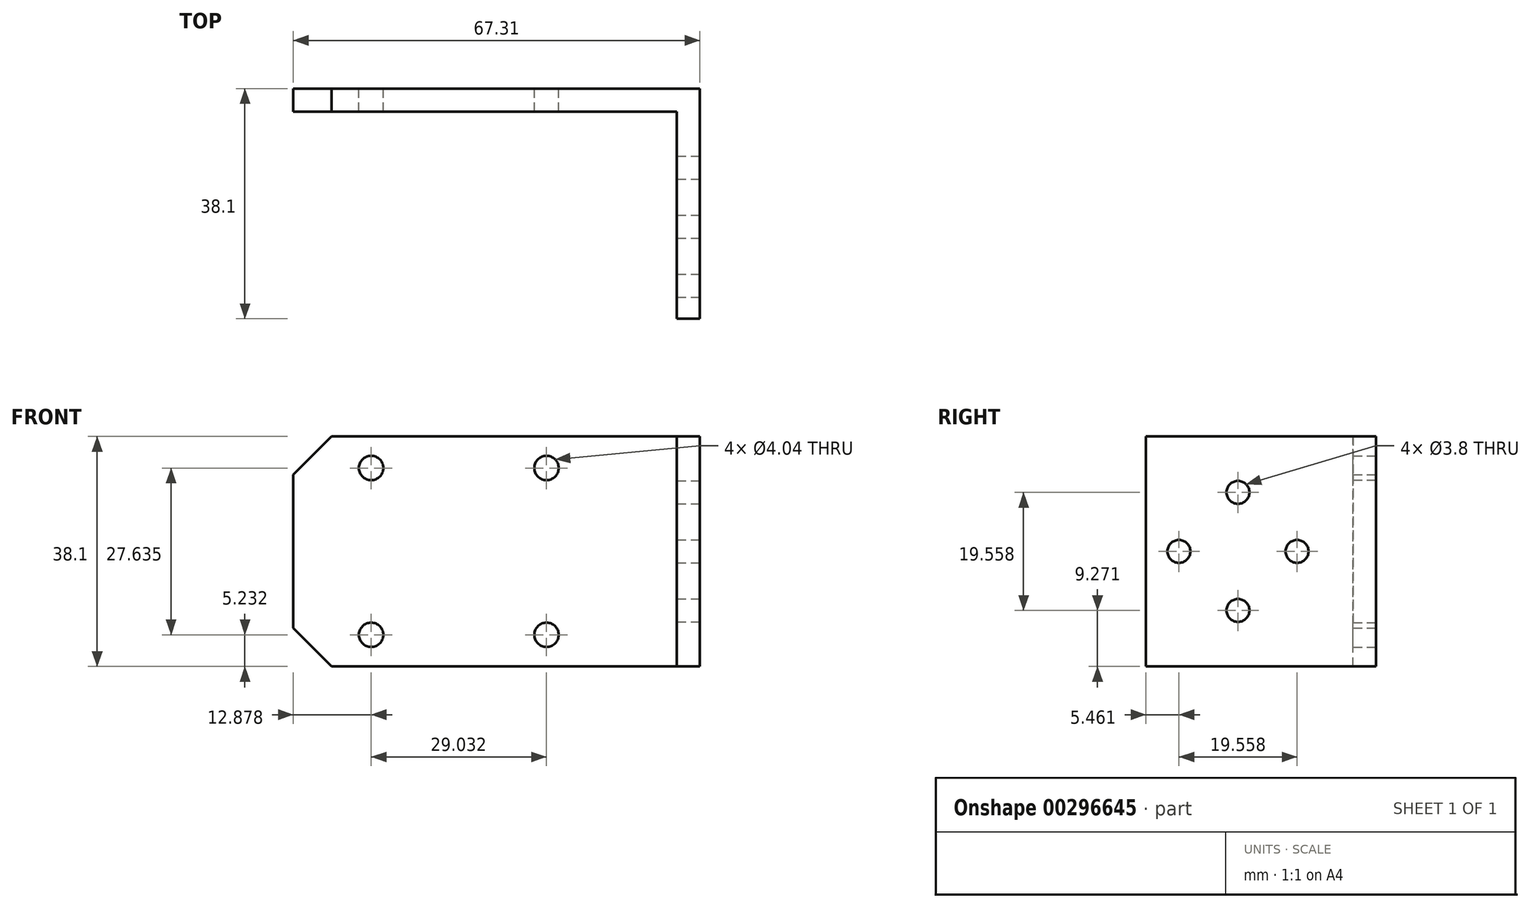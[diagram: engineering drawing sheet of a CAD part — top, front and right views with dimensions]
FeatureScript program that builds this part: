
annotation { "Feature Type Name" : "Feature", "Feature Type Description" : "" }
export const myFeature = defineFeature(function(context is Context, id is Id, definition is map)
    precondition{}
    {
        {
            var Q0;
            Q0=qCreatedBy(makeId("Front.planeOp"),FACE);
            var sketch = newSketch(context, id + "F0", { "sketchPlane" : qUnion([Q0])});
            skLineSegment(sketch, "E0", {"start": v(0, 19.05) * mm, "end": v(-57.15, 19.05) * mm});
            skLineSegment(sketch, "E1", {"start": v(-57.15, 19.05) * mm, "end": v(-63.5, 12.7) * mm});
            skLineSegment(sketch, "E2", {"start": v(-63.5, 12.7) * mm, "end": v(-63.5, 0) * mm});
            skLineSegment(sketch, "E3.bottom", {"start": v(0, 19.05) * mm, "end": v(3.81, 19.05) * mm});
            skLineSegment(sketch, "E3.left", {"start": v(0, 19.05) * mm, "end": v(0, 0) * mm});
            skLineSegment(sketch, "E3.right", {"start": v(3.8, 19.05) * mm, "end": v(3.81, 0) * mm});
            skCircle(sketch, "E4", {"center": v(-50.62, 13.82) * mm, "radius": 2.02 * mm});
            skCircle(sketch, "E5", {"center": v(-21.59, 13.82) * mm, "radius": 2.02 * mm});
            skCircle(sketch, "E6.MirrorC", {"center": v(-21.59, -13.82) * mm, "radius": 2.02 * mm});
            skLineSegment(sketch, "E7.MirrorCS", {"start": v(-57.15, -19.05) * mm, "end": v(-63.5, -12.7) * mm});
            skCircle(sketch, "E8.MirrorC", {"center": v(-50.62, -13.82) * mm, "radius": 2.02 * mm});
            skLineSegment(sketch, "E9.MirrorCS", {"start": v(0, -19.05) * mm, "end": v(-57.15, -19.05) * mm});
            skLineSegment(sketch, "E10.MirrorCS", {"start": v(3.8, -19.05) * mm, "end": v(3.81, 0) * mm});
            skLineSegment(sketch, "E11.MirrorCS", {"start": v(0, -19.05) * mm, "end": v(3.81, -19.05) * mm});
            skLineSegment(sketch, "E12.MirrorCS", {"start": v(0, -19.05) * mm, "end": v(0, 0) * mm});
            skLineSegment(sketch, "E13.MirrorCS", {"start": v(-63.5, -12.7) * mm, "end": v(-63.5, 0) * mm});
            skSolve(sketch);
        }
        {
            var Q0;
            Q0=makeQuery(id+"F0.imprint","IMPRINT",FACE,{"disambiguationData":[TD([[makeQuery(id+"F0.imprint","IMPRINT",EDGE,{"derivedFrom":sQuery(id+"F0.wireOp",EDGE,"E0")}),1.0]])]});
            extrude(context, id + "F1", {"entities" : qUnion([Q0]), "depth" : 3.8 * mm});
        }
        {
            var Q0;
            Q0=makeQuery(id+"F0.imprint","IMPRINT",FACE,{"disambiguationData":[TD([[makeQuery(id+"F0.imprint","IMPRINT",EDGE,{"derivedFrom":sQuery(id+"F0.wireOp",EDGE,"E3.bottom")}),-1.0]])]});
            extrude(context, id + "F2", {"entities" : qUnion([Q0]), "operationType" : NewBodyOperationType.ADD, "depth" : 38.1 * mm});
        }
        {
            var Q0;
            Q0=makeQuery(id+"F2.opExtrude","SWEPT_FACE",FACE,{"disambiguationData":[OSD([sQuery(id+"F0.wireOp",EDGE,"E3.right"),sQuery(id+"F0.wireOp",EDGE,"E10.MirrorCS")])]});
            var sketch = newSketch(context, id + "F3", { "sketchPlane" : qUnion([Q0])});
            skPoint(sketch, "E14", {"position": v(-22.86, 0) * mm});
            skCircle(sketch, "E15", {"center": v(-22.86, 0) * mm, "radius": 9.78 * mm, "construction": true});
            skCircle(sketch, "E16", {"center": v(-22.86, 9.78) * mm, "radius": 1.9 * mm});
            skCircle(sketch, "E17.MirrorC", {"center": v(-22.86, -9.78) * mm, "radius": 1.9 * mm});
            skCircle(sketch, "E18", {"center": v(-32.64, 0) * mm, "radius": 1.9 * mm});
            skLineSegment(sketch, "E19", {"start": v(-22.86, 9.78) * mm, "end": v(-22.86, -9.78) * mm, "construction": true});
            skCircle(sketch, "E20.MirrorC", {"center": v(-13.08, 0) * mm, "radius": 1.9 * mm});
            skSolve(sketch);
        }
        {
            var Q0;
            Q0 = qSketchRegion(id + "F3", true);
            extrude(context, id + "F4", {"entities" : qUnion([Q0]), "operationType" : NewBodyOperationType.REMOVE, "endBound" : BoundingType.THROUGH_ALL, "oppositeDirection" : true, "depth" : 25.4 * mm});
        }
    });
